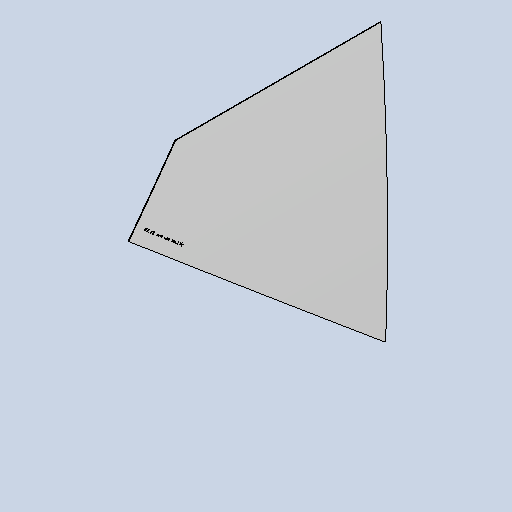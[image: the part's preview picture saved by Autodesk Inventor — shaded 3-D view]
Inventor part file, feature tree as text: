
AUTODESK INVENTOR PART (.ipt)
format: ipt  version: 2025 (Build 290162010, 162A)  size: 513,024 bytes
history: native  units: mm
features: sheet_metal_op x3, other x3, sketch x3, extrude x1, fillet x1, projected_geometry x1
ambient origin geometry x8: Origin, YZ Plane, XZ Plane, XY Plane, X Axis, Y Axis, Z Axis, Center Point
bodies: Body1 (feature_tree)
feature tree (12):
  sheet_metal_op  "Contour Flange2"
  extrude  "Extrusion2"  Depth=3.0mm
  fillet  "Fillet1"  Radius=1.5mm
  other  "Mark1"
  sketch  "Sketch1"  dims[d36=3.0mm d37=3.0mm d38=1.5mm]
  other  "Plate2"
  sheet_metal_op  "Bend2"
  sheet_metal_op  "Corner2"
  sketch  "Sketch2"  dims[d39=6.0mm]
  projected_geometry  "Projected Loop1"
  sketch  "Sketch3"  dims[d40=5.0mm d41=1250.0mm d42=5.0mm d43=3.0mm d44=12.0mm d45=3.0mm d46=5.0mm d54=1500.0mm d55=2700.0mm d58=2100.0mm d65=8.0mm d66=8.0mm d68=8.0mm d69=3.0mm d70=3.0mm d75=3.0mm d78=3.0mm d80=3.0mm d83=8.0mm d86=3.0mm d112=241.9mm d113=50.0mm d114=50.0mm d115=3.0mm d116=25.0mm d117=110.0mm d118=25.0mm d119=92.8mm d130=10.0mm d131=0.0mm d152=1286.0mm d153=290.0mm d173=345.609mm d174=3.0mm d176=12.0mm d177=200.0mm d178=50.0mm d179=50.0mm]
  other  "Definition1"
